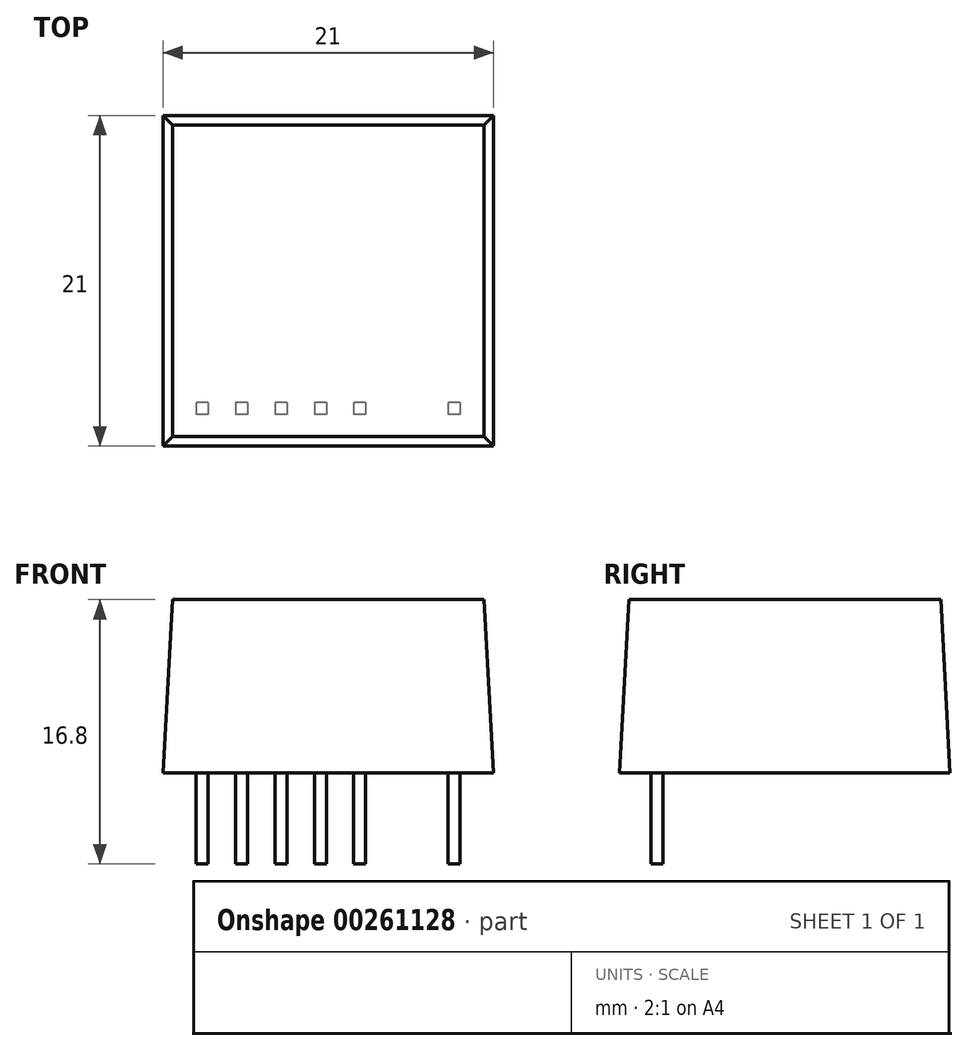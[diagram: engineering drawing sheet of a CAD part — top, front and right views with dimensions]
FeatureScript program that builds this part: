
annotation { "Feature Type Name" : "Feature", "Feature Type Description" : "" }
export const myFeature = defineFeature(function(context is Context, id is Id, definition is map)
    precondition{}
    {
        {
            var Q0;
            Q0=qCreatedBy(makeId("Top.planeOp"),FACE);
            var sketch = newSketch(context, id + "F0", { "sketchPlane" : qUnion([Q0])});
            skLineSegment(sketch, "E0.bottom", {"start": v(21, 0) * mm, "end": v(0, 0) * mm});
            skLineSegment(sketch, "E0.top", {"start": v(21, 21) * mm, "end": v(0, 21) * mm});
            skLineSegment(sketch, "E0.left", {"start": v(21, 0) * mm, "end": v(21, 21) * mm});
            skLineSegment(sketch, "E0.right", {"start": v(0, 0) * mm, "end": v(0, 21) * mm});
            skPoint(sketch, "E0.middle", {"position": v(10.5, 10.5) * mm});
            skSolve(sketch);
        }
        {
            var Q0;
            Q0 = qSketchRegion(id + "F0", true);
            extrude(context, id + "F1", {"entities" : qUnion([Q0]), "depth" : 11 * mm});
        }
        {
            var Q0;
            Q0=makeQuery(id+"F1.opExtrude","SWEPT_FACE",FACE,{"disambiguationData":[OSD([sQuery(id+"F0.wireOp",EDGE,"E0.bottom")])]});
            var sketch = newSketch(context, id + "F2", { "sketchPlane" : qUnion([Q0])});
            skLineSegment(sketch, "E1", {"start": v(0, 0) * mm, "end": v(0.6, 11) * mm});
            skLineSegment(sketch, "E2", {"start": v(0.6, 11) * mm, "end": v(0, 11) * mm});
            skLineSegment(sketch, "E3", {"start": v(0, 11) * mm, "end": v(0, 0) * mm});
            skLineSegment(sketch, "E4", {"start": v(21, 0) * mm, "end": v(21, 11) * mm});
            skLineSegment(sketch, "E5", {"start": v(21, 11) * mm, "end": v(20.4, 11) * mm});
            skLineSegment(sketch, "E6", {"start": v(20.4, 11) * mm, "end": v(21, 0) * mm});
            skSolve(sketch);
        }
        {
            var Q0;
            Q0 = qSketchRegion(id + "F2", true);
            var Q1;
            Q1 = qConstructionFilter(qBodyType(qCreatedBy(id + "F2" ,EDGE), BodyType.WIRE), ConstructionObject.NO);
            extrude(context, id + "F3", {"entities" : qUnion([Q0]), "operationType" : NewBodyOperationType.REMOVE, "surfaceEntities" : qUnion([Q1]), "endBound" : BoundingType.THROUGH_ALL, "oppositeDirection" : true, "depth" : 25 * mm});
        }
        {
            var Q0;
            Q0=qCreatedBy(makeId("Right.planeOp"),FACE);
            var sketch = newSketch(context, id + "F4", { "sketchPlane" : qUnion([Q0])});
            skLineSegment(sketch, "E7", {"start": v(21, 0) * mm, "end": v(21, 11) * mm});
            skLineSegment(sketch, "E8", {"start": v(21, 11) * mm, "end": v(20.4, 11) * mm});
            skLineSegment(sketch, "E9", {"start": v(20.4, 11) * mm, "end": v(21, 0) * mm});
            skLineSegment(sketch, "E10", {"start": v(0, 0) * mm, "end": v(0, 11) * mm});
            skLineSegment(sketch, "E11", {"start": v(0, 11) * mm, "end": v(0.6, 11) * mm});
            skLineSegment(sketch, "E12", {"start": v(0.6, 11) * mm, "end": v(0, 0) * mm});
            skSolve(sketch);
        }
        {
            var Q0;
            Q0 = qSketchRegion(id + "F4", true);
            extrude(context, id + "F5", {"entities" : qUnion([Q0]), "operationType" : NewBodyOperationType.REMOVE, "depth" : 25 * mm});
        }
        {
            var Q0;
            Q0=makeQuery(id+"F1.opExtrude","CAP_FACE",FACE,{"disambiguationData":[OSD([sQuery(id+"F0.wireOp",EDGE,"E0.bottom"),sQuery(id+"F0.wireOp",EDGE,"E0.top"),sQuery(id+"F0.wireOp",EDGE,"E0.left"),sQuery(id+"F0.wireOp",EDGE,"E0.right")])],"isStart":true});
            var sketch = newSketch(context, id + "F6", { "sketchPlane" : qUnion([Q0])});
            skLineSegment(sketch, "E13", {"start": v(0, 0) * mm, "end": v(21, 0) * mm});
            skLineSegment(sketch, "E14", {"start": v(21, 0) * mm, "end": v(21, -21) * mm});
            skLineSegment(sketch, "E15", {"start": v(21, -21) * mm, "end": v(0, -21) * mm});
            skLineSegment(sketch, "E16", {"start": v(0, -21) * mm, "end": v(0, 0) * mm});
            skLineSegment(sketch, "E17.bottom", {"start": v(2.88, -2.76) * mm, "end": v(2.12, -2.76) * mm});
            skLineSegment(sketch, "E17.top", {"start": v(2.88, -2) * mm, "end": v(2.12, -2) * mm});
            skLineSegment(sketch, "E17.left", {"start": v(2.88, -2.76) * mm, "end": v(2.88, -2) * mm});
            skLineSegment(sketch, "E17.right", {"start": v(2.12, -2.76) * mm, "end": v(2.12, -2) * mm});
            skPoint(sketch, "E17.middle", {"position": v(2.5, -2.38) * mm});
            skLineSegment(sketch, "E18.bottom", {"start": v(5.38, -2.76) * mm, "end": v(4.62, -2.76) * mm});
            skLineSegment(sketch, "E18.top", {"start": v(5.38, -2) * mm, "end": v(4.62, -2) * mm});
            skLineSegment(sketch, "E18.left", {"start": v(5.38, -2.76) * mm, "end": v(5.38, -2) * mm});
            skLineSegment(sketch, "E18.right", {"start": v(4.62, -2.76) * mm, "end": v(4.62, -2) * mm});
            skPoint(sketch, "E18.middle", {"position": v(5, -2.38) * mm});
            skLineSegment(sketch, "E19.bottom", {"start": v(7.88, -2.76) * mm, "end": v(7.12, -2.76) * mm});
            skLineSegment(sketch, "E19.top", {"start": v(7.88, -2) * mm, "end": v(7.12, -2) * mm});
            skLineSegment(sketch, "E19.left", {"start": v(7.88, -2.76) * mm, "end": v(7.88, -2) * mm});
            skLineSegment(sketch, "E19.right", {"start": v(7.12, -2.76) * mm, "end": v(7.12, -2) * mm});
            skPoint(sketch, "E19.middle", {"position": v(7.5, -2.38) * mm});
            skLineSegment(sketch, "E20.bottom", {"start": v(10.38, -2.76) * mm, "end": v(9.62, -2.76) * mm});
            skLineSegment(sketch, "E20.top", {"start": v(10.38, -2) * mm, "end": v(9.62, -2) * mm});
            skLineSegment(sketch, "E20.left", {"start": v(10.38, -2.76) * mm, "end": v(10.38, -2) * mm});
            skLineSegment(sketch, "E20.right", {"start": v(9.62, -2.76) * mm, "end": v(9.62, -2) * mm});
            skPoint(sketch, "E20.middle", {"position": v(10, -2.38) * mm});
            skLineSegment(sketch, "E21.bottom", {"start": v(12.88, -2.76) * mm, "end": v(12.12, -2.76) * mm});
            skLineSegment(sketch, "E21.top", {"start": v(12.88, -2) * mm, "end": v(12.12, -2) * mm});
            skLineSegment(sketch, "E21.left", {"start": v(12.88, -2.76) * mm, "end": v(12.88, -2) * mm});
            skLineSegment(sketch, "E21.right", {"start": v(12.12, -2.76) * mm, "end": v(12.12, -2) * mm});
            skPoint(sketch, "E21.middle", {"position": v(12.5, -2.38) * mm});
            skLineSegment(sketch, "E22.bottom", {"start": v(18.88, -2.76) * mm, "end": v(18.12, -2.76) * mm});
            skLineSegment(sketch, "E22.top", {"start": v(18.88, -2) * mm, "end": v(18.12, -2) * mm});
            skLineSegment(sketch, "E22.left", {"start": v(18.88, -2.76) * mm, "end": v(18.88, -2) * mm});
            skLineSegment(sketch, "E22.right", {"start": v(18.12, -2.76) * mm, "end": v(18.12, -2) * mm});
            skPoint(sketch, "E22.middle", {"position": v(18.5, -2.38) * mm});
            skSolve(sketch);
        }
        {
            var Q0;
            Q0=makeQuery(id+"F6.imprint","IMPRINT",FACE,{"disambiguationData":[TD([[makeQuery(id+"F6.imprint","IMPRINT",EDGE,{"derivedFrom":sQuery(id+"F6.wireOp",EDGE,"E17.bottom")}),-1.0]])]});
            var Q1;
            Q1=makeQuery(id+"F6.imprint","IMPRINT",FACE,{"disambiguationData":[TD([[makeQuery(id+"F6.imprint","IMPRINT",EDGE,{"derivedFrom":sQuery(id+"F6.wireOp",EDGE,"E18.bottom")}),-1.0]])]});
            var Q2;
            Q2=makeQuery(id+"F6.imprint","IMPRINT",FACE,{"disambiguationData":[TD([[makeQuery(id+"F6.imprint","IMPRINT",EDGE,{"derivedFrom":sQuery(id+"F6.wireOp",EDGE,"E19.bottom")}),-1.0]])]});
            var Q3;
            Q3=makeQuery(id+"F6.imprint","IMPRINT",FACE,{"disambiguationData":[TD([[makeQuery(id+"F6.imprint","IMPRINT",EDGE,{"derivedFrom":sQuery(id+"F6.wireOp",EDGE,"E20.bottom")}),-1.0]])]});
            var Q4;
            Q4=makeQuery(id+"F6.imprint","IMPRINT",FACE,{"disambiguationData":[TD([[makeQuery(id+"F6.imprint","IMPRINT",EDGE,{"derivedFrom":sQuery(id+"F6.wireOp",EDGE,"E21.bottom")}),-1.0]])]});
            var Q5;
            Q5=makeQuery(id+"F6.imprint","IMPRINT",FACE,{"disambiguationData":[TD([[makeQuery(id+"F6.imprint","IMPRINT",EDGE,{"derivedFrom":sQuery(id+"F6.wireOp",EDGE,"E22.bottom")}),-1.0]])]});
            extrude(context, id + "F7", {"entities" : qUnion([Q0, Q1, Q2, Q3, Q4, Q5]), "operationType" : NewBodyOperationType.ADD, "depth" : 5.8 * mm});
        }
    });
